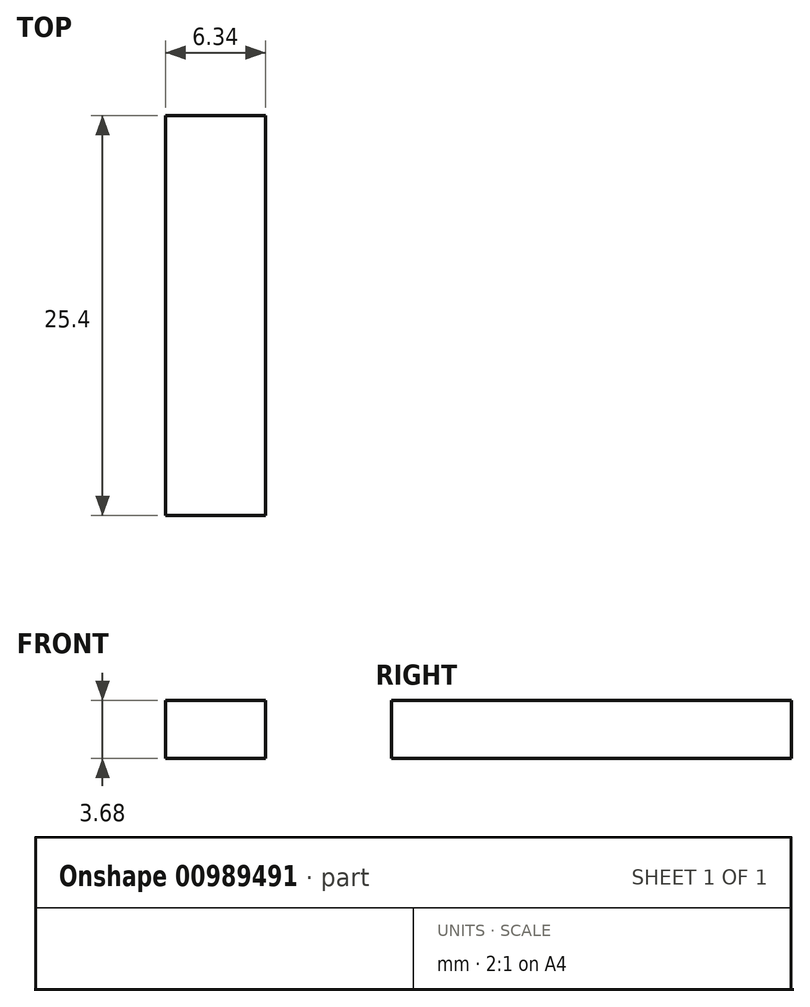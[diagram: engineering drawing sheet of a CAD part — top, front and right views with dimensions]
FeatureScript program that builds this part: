
annotation { "Feature Type Name" : "Feature", "Feature Type Description" : "" }
export const myFeature = defineFeature(function(context is Context, id is Id, definition is map)
    precondition{}
    {
        {
            var Q0;
            Q0=qCreatedBy(makeId("Front.planeOp"),FACE);
            var sketch = newSketch(context, id + "F0", { "sketchPlane" : qUnion([Q0])});
            skLineSegment(sketch, "E0.bottom", {"start": v(-3.17, 1.84) * mm, "end": v(3.18, 1.84) * mm});
            skLineSegment(sketch, "E0.top", {"start": v(-3.17, -1.84) * mm, "end": v(3.17, -1.84) * mm});
            skLineSegment(sketch, "E0.left", {"start": v(-3.17, 1.84) * mm, "end": v(-3.17, -1.84) * mm});
            skLineSegment(sketch, "E0.right", {"start": v(3.18, 1.84) * mm, "end": v(3.18, -1.84) * mm});
            skPoint(sketch, "E0.middle", {"position": v(0, 0) * mm});
            skSolve(sketch);
        }
        {
            var Q0;
            Q0=makeQuery(id+"F0.imprint","IMPRINT",FACE,{"disambiguationData":[TD([[makeQuery(id+"F0.imprint","IMPRINT",EDGE,{"derivedFrom":sQuery(id+"F0.wireOp",EDGE,"E0.bottom")}),-1.0]])]});
            extrude(context, id + "F1", {"entities" : qUnion([Q0]), "depth" : 25.4 * mm, "offsetDistance" : 25.4 * mm});
        }
    });
